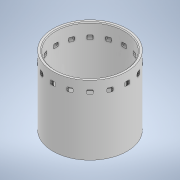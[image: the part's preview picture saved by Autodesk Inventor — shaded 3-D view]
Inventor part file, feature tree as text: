
AUTODESK INVENTOR PART (.ipt)
format: ipt  version: 2022.4 (Build 264492010, 492A)  size: 335,872 bytes
history: native  units: mm
features: extrude x2, sketch x2, fillet x1, chamfer x1, pattern_circular x1, plane x1
ambient origin geometry x8: Origin, YZ Plane, XZ Plane, XY Plane, X Axis, Y Axis, Z Axis, Center Point
bodies: Solid1 (feature_tree)
feature tree (8):
  extrude  "Extrusion1"  Depth=85.0mm TaperAngle=0.0deg
  extrude  "Extrusion3"  Depth=1.0mm
  fillet  "Fillet1"  [1 undecoded]
  chamfer  "Chamfer1"  Distance=10.0mm
  pattern_circular  "Circular Pattern2"  [2 undecoded]
  plane  "Work Plane1"
  sketch  "Sketch1"  dims[d0=84.05mm d2=85.0mm d3=0.0mm]
  sketch  "Sketch2"  dims[d4=5.0mm d5=5.0mm d8=45.0deg d9=10.0mm d10=6.0mm d11=0.0mm d12=1.0mm d16=1.0mm d17=2.0mm d18=45.0deg d19=160.0mm d20=360.0deg d24=43.0mm d38=3.5mm]
note: 3 required parameter values undecoded (feature->parameter linkage not recoverable at this tier; creation-order binding heuristic only, values carry confidence <= 0.55)
